# Revit family: Cambio Wall Systems - Lighting - Geometric 9 Circles
name_source: partatom
category: Generic Models
units: mm (PartAtom-declared; Revit-internal decimal feet)

## family parameters
Can host rebar = No
Cut with Voids When Loaded = No
Host = Face
Maintain Annotation Orientation = No
Part Type = Normal
Room Calculation Point = No
Round Connector Dimension = Use Diameter
Shared = No

## types (6) — shared parameters
Default Elevation = 4' - 0"

## per-type parameters (varying)
| type | Cambio Material |
| Panel Color - COBALT | Cambio Lighting - Geometric - Cobalt |
| Panel Color - JET | Cambio Lighting - Geometric - Jet |
| Panel Color - LIGHT GREY | Cambio Lighting - Geometric - Light Grey |
| Panel Color - LIME | Cambio Lighting - Geometric - Lime |
| Panel Color - ORANGE | Cambio Lighting - Geometric - Orange |
| Panel Color - PEWTER | Cambio Lighting - Geometric - Pewter |

## geometry (parser evidence)
native form markers: Sweep x1
no freeform markers — native parametric forms only
